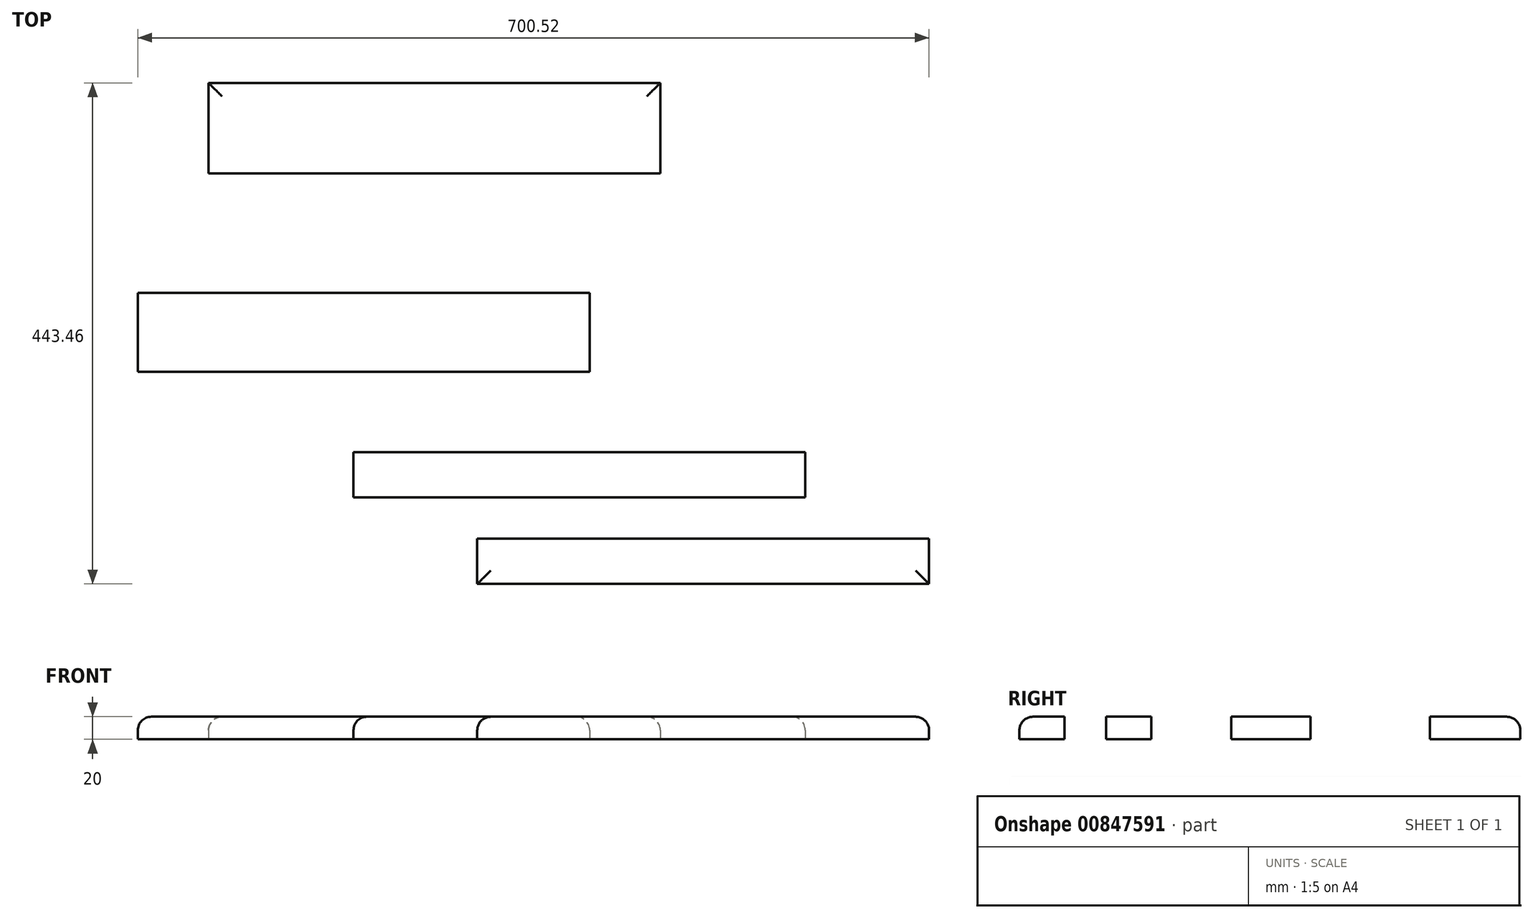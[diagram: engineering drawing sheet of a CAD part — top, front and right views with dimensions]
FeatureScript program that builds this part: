
annotation { "Feature Type Name" : "Feature", "Feature Type Description" : "" }
export const myFeature = defineFeature(function(context is Context, id is Id, definition is map)
    precondition{}
    {
        {
            var Q0;
            Q0=qCreatedBy(makeId("Top.planeOp"),FACE);
            var sketch = newSketch(context, id + "F0", { "sketchPlane" : qUnion([Q0])});
            skLineSegment(sketch, "E0.bottom", {"start": v(-256.47, -93.17) * mm, "end": v(143.53, -93.17) * mm});
            skLineSegment(sketch, "E0.top", {"start": v(-256.47, -133.17) * mm, "end": v(143.53, -133.17) * mm});
            skLineSegment(sketch, "E0.left", {"start": v(-256.47, -93.17) * mm, "end": v(-256.47, -133.17) * mm});
            skLineSegment(sketch, "E0.right", {"start": v(143.53, -93.17) * mm, "end": v(143.53, -133.17) * mm});
            skSolve(sketch);
        }
        {
            var Q0;
            Q0=qCreatedBy(makeId("Top.planeOp"),FACE);
            var sketch = newSketch(context, id + "F1", { "sketchPlane" : qUnion([Q0])});
            skLineSegment(sketch, "E1.bottom", {"start": v(-366.04, -16.5) * mm, "end": v(33.96, -16.5) * mm});
            skLineSegment(sketch, "E1.top", {"start": v(-366.04, -56.5) * mm, "end": v(33.96, -56.5) * mm});
            skLineSegment(sketch, "E1.left", {"start": v(-366.04, -16.5) * mm, "end": v(-366.04, -56.5) * mm});
            skLineSegment(sketch, "E1.right", {"start": v(33.96, -16.5) * mm, "end": v(33.96, -56.5) * mm});
            skSolve(sketch);
        }
        {
            var Q0;
            Q0=qCreatedBy(makeId("Top.planeOp"),FACE);
            var sketch = newSketch(context, id + "F2", { "sketchPlane" : qUnion([Q0])});
            skLineSegment(sketch, "E2.bottom", {"start": v(-556.99, 124.48) * mm, "end": v(-156.99, 124.48) * mm});
            skLineSegment(sketch, "E2.top", {"start": v(-556.99, 54.48) * mm, "end": v(-156.99, 54.48) * mm});
            skLineSegment(sketch, "E2.left", {"start": v(-556.99, 124.48) * mm, "end": v(-556.99, 54.48) * mm});
            skLineSegment(sketch, "E2.right", {"start": v(-156.99, 124.48) * mm, "end": v(-156.99, 54.48) * mm});
            skSolve(sketch);
        }
        {
            var Q0;
            Q0=qCreatedBy(makeId("Top.planeOp"),FACE);
            var sketch = newSketch(context, id + "F3", { "sketchPlane" : qUnion([Q0])});
            skLineSegment(sketch, "E3.bottom", {"start": v(-494.4, 310.3) * mm, "end": v(-94.4, 310.3) * mm});
            skLineSegment(sketch, "E3.top", {"start": v(-494.4, 230.3) * mm, "end": v(-94.4, 230.3) * mm});
            skLineSegment(sketch, "E3.left", {"start": v(-494.4, 310.3) * mm, "end": v(-494.4, 230.3) * mm});
            skLineSegment(sketch, "E3.right", {"start": v(-94.4, 310.3) * mm, "end": v(-94.4, 230.3) * mm});
            skSolve(sketch);
        }
        {
            var Q0;
            Q0 = qSketchRegion(id + "F0", true);
            extrude(context, id + "F4", {"entities" : qUnion([Q0]), "depth" : 20 * mm, "offsetDistance" : 25 * mm});
        }
        {
            var Q0;
            Q0 = qSketchRegion(id + "F1", true);
            extrude(context, id + "F5", {"entities" : qUnion([Q0]), "depth" : 20 * mm, "offsetDistance" : 25 * mm});
        }
        {
            var Q0;
            Q0 = qSketchRegion(id + "F2", true);
            extrude(context, id + "F6", {"entities" : qUnion([Q0]), "depth" : 20 * mm, "offsetDistance" : 25 * mm});
        }
        {
            var Q0;
            Q0 = qSketchRegion(id + "F3", true);
            extrude(context, id + "F7", {"entities" : qUnion([Q0]), "depth" : 20 * mm, "offsetDistance" : 25 * mm});
        }
        {
            var Q0;
            Q0=makeQuery(id+"F7.opExtrude","CAP_EDGE",EDGE,{"disambiguationData":[OSD([sQuery(id+"F3.wireOp",EDGE,"E3.bottom")])],"isStart":false});
            var Q1;
            Q1=makeQuery(id+"F7.opExtrude","CAP_EDGE",EDGE,{"disambiguationData":[OSD([sQuery(id+"F3.wireOp",EDGE,"E3.right")])],"isStart":false});
            var Q2;
            Q2=makeQuery(id+"F7.opExtrude","CAP_EDGE",EDGE,{"disambiguationData":[OSD([sQuery(id+"F3.wireOp",EDGE,"E3.left")])],"isStart":false});
            var Q3;
            Q3=makeQuery(id+"F6.opExtrude","CAP_EDGE",EDGE,{"disambiguationData":[OSD([sQuery(id+"F2.wireOp",EDGE,"E2.left")])],"isStart":false});
            var Q4;
            Q4=makeQuery(id+"F6.opExtrude","CAP_EDGE",EDGE,{"disambiguationData":[OSD([sQuery(id+"F2.wireOp",EDGE,"E2.right")])],"isStart":false});
            var Q5;
            Q5=makeQuery(id+"F5.opExtrude","CAP_EDGE",EDGE,{"disambiguationData":[OSD([sQuery(id+"F1.wireOp",EDGE,"E1.left")])],"isStart":false});
            var Q6;
            Q6=makeQuery(id+"F5.opExtrude","CAP_EDGE",EDGE,{"disambiguationData":[OSD([sQuery(id+"F1.wireOp",EDGE,"E1.right")])],"isStart":false});
            var Q7;
            Q7=makeQuery(id+"F4.opExtrude","CAP_EDGE",EDGE,{"disambiguationData":[OSD([sQuery(id+"F0.wireOp",EDGE,"E0.left")])],"isStart":false});
            var Q8;
            Q8=makeQuery(id+"F4.opExtrude","CAP_EDGE",EDGE,{"disambiguationData":[OSD([sQuery(id+"F0.wireOp",EDGE,"E0.right")])],"isStart":false});
            var Q9;
            Q9=makeQuery(id+"F4.opExtrude","CAP_EDGE",EDGE,{"disambiguationData":[OSD([sQuery(id+"F0.wireOp",EDGE,"E0.top")])],"isStart":false});
            fillet(context, id + "F8", {"entities" : qUnion([Q0, Q1, Q2, Q3, Q4, Q5, Q6, Q7, Q8, Q9]), "radius" : 12 * mm, "tangentPropagation" : true, "allowEdgeOverflow" : false});
        }
    });
